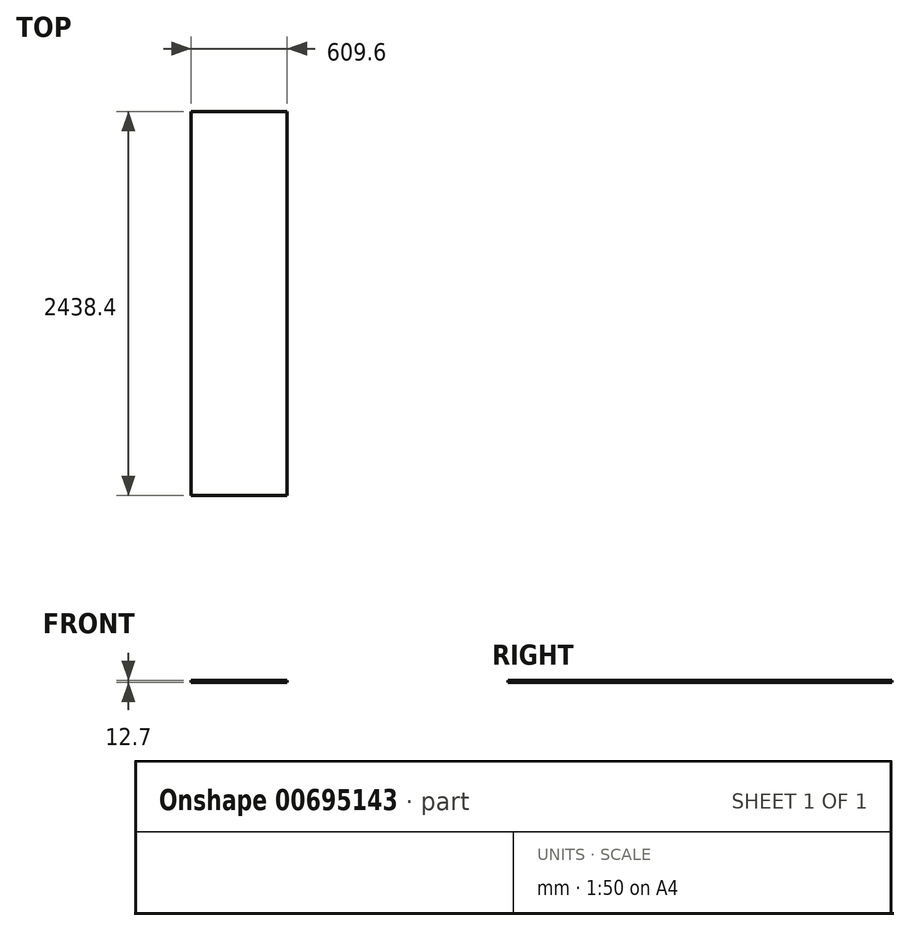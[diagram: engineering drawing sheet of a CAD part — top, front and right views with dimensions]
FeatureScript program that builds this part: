
annotation { "Feature Type Name" : "Feature", "Feature Type Description" : "" }
export const myFeature = defineFeature(function(context is Context, id is Id, definition is map)
    precondition{}
    {
        {
            var Q0;
            Q0=qCreatedBy(makeId("Top.planeOp"),FACE);
            var sketch = newSketch(context, id + "F0", { "sketchPlane" : qUnion([Q0])});
            skLineSegment(sketch, "E0.bottom", {"start": v(111.22, -2194.04) * mm, "end": v(720.82, -2194.04) * mm});
            skLineSegment(sketch, "E0.top", {"start": v(111.22, 244.36) * mm, "end": v(720.82, 244.36) * mm});
            skLineSegment(sketch, "E0.left", {"start": v(111.22, -2194.04) * mm, "end": v(111.22, 244.36) * mm});
            skLineSegment(sketch, "E0.right", {"start": v(720.82, -2194.04) * mm, "end": v(720.82, 244.36) * mm});
            skSolve(sketch);
        }
        {
            var Q0;
            Q0=makeQuery(id+"F0.imprint","IMPRINT",FACE,{"disambiguationData":[TD([[makeQuery(id+"F0.imprint","IMPRINT",EDGE,{"derivedFrom":sQuery(id+"F0.wireOp",EDGE,"E0.bottom")}),1.0]])]});
            extrude(context, id + "F1", {"entities" : qUnion([Q0]), "depth" : 12.7 * mm, "offsetDistance" : 25.4 * mm});
        }
    });
